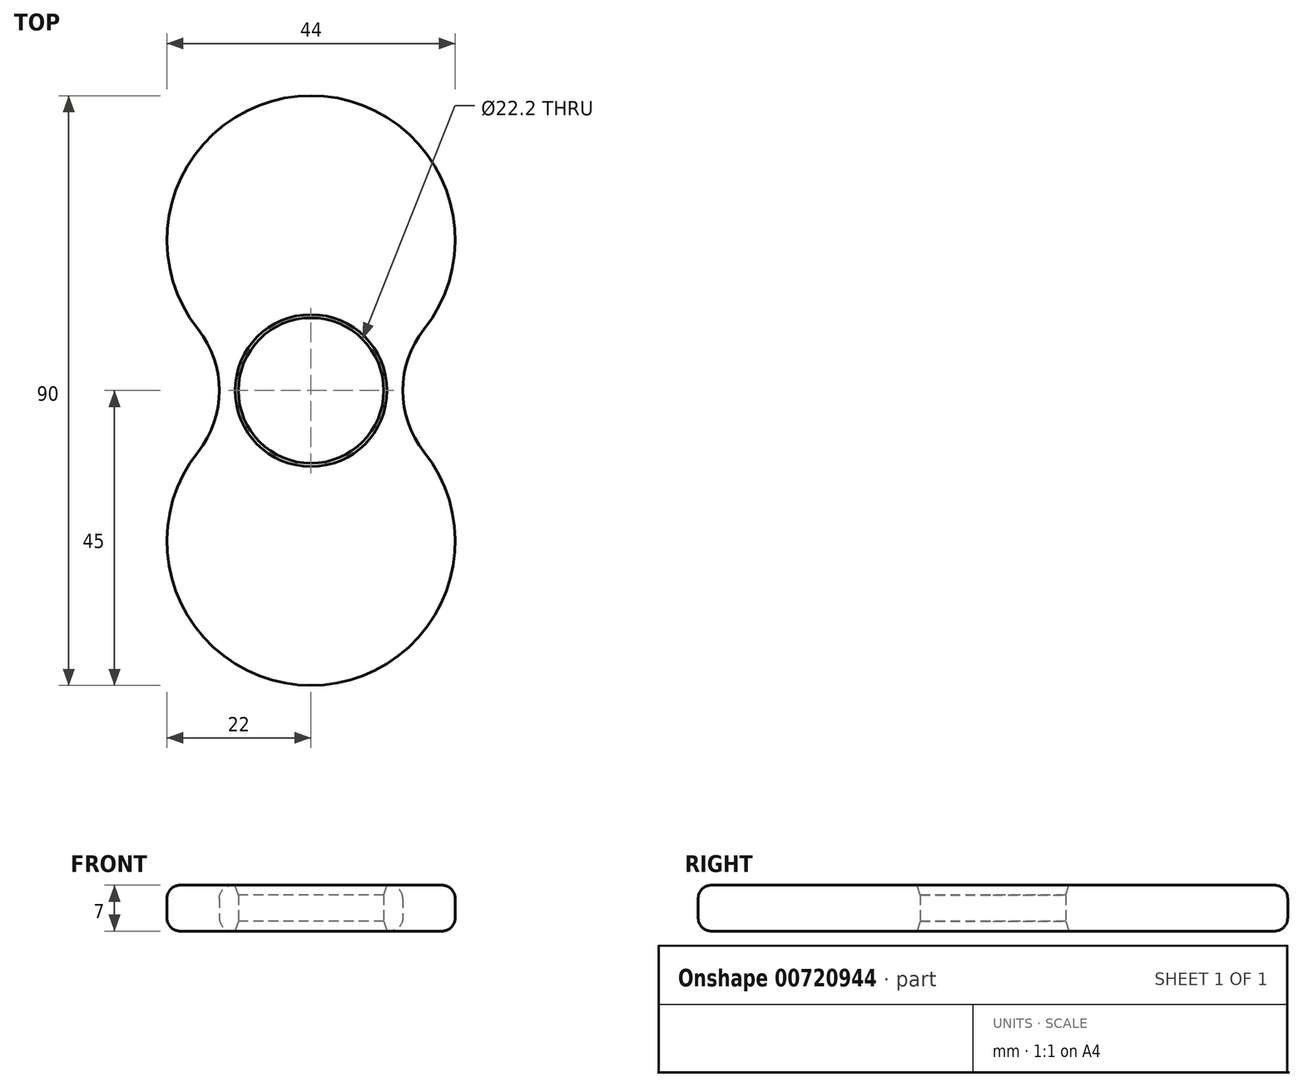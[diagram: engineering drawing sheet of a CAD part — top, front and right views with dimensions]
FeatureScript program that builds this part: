
annotation { "Feature Type Name" : "Feature", "Feature Type Description" : "" }
export const myFeature = defineFeature(function(context is Context, id is Id, definition is map)
    precondition{}
    {
        {
            var Q0;
            Q0=qCreatedBy(makeId("Top.planeOp"),FACE);
            var sketch = newSketch(context, id + "F0", { "sketchPlane" : qUnion([Q0])});
            skLineSegment(sketch, "E0", {"start": v(0, 0) * mm, "end": v(-28, 0) * mm, "construction": true});
            skArc(sketch, "E1", {"start": v(-31.25, -9.35) * mm, "mid": v(-28, 0) * mm, "end": v(-31.25, 9.35) * mm});
            skArc(sketch, "E2", {"start": v(3.25, 9.35) * mm, "mid": v(0, 0) * mm, "end": v(3.25, -9.35) * mm});
            skArc(sketch, "E3", {"start": v(3.25, 9.35) * mm, "mid": v(-14, 45) * mm, "end": v(-31.25, 9.35) * mm});
            skArc(sketch, "E4", {"start": v(-31.25, -9.35) * mm, "mid": v(-14, -45) * mm, "end": v(3.25, -9.35) * mm});
            skLineSegment(sketch, "E5", {"start": v(-36, 23) * mm, "end": v(8, 23) * mm, "construction": true});
            skLineSegment(sketch, "E6", {"start": v(-14, 45) * mm, "end": v(-14, -45) * mm, "construction": true});
            skCircle(sketch, "E7", {"center": v(-14, 0) * mm, "radius": 11.1 * mm});
            skSolve(sketch);
        }
        {
            var Q0;
            Q0=makeQuery(id+"F0.imprint","IMPRINT",FACE,{"disambiguationData":[TD([[makeQuery(id+"F0.imprint","IMPRINT",EDGE,{"derivedFrom":sQuery(id+"F0.wireOp",EDGE,"E1")}),-1.0]])]});
            extrude(context, id + "F1", {"entities" : qUnion([Q0]), "depth" : 7 * mm});
        }
        {
            var Q0;
            Q0=makeQuery(id+"F1.opExtrude","CAP_EDGE",EDGE,{"disambiguationData":[OSD([sQuery(id+"F0.wireOp",EDGE,"E7")])],"isStart":false});
            var Q1;
            Q1=makeQuery(id+"F1.opExtrude","CAP_EDGE",EDGE,{"disambiguationData":[OSD([sQuery(id+"F0.wireOp",EDGE,"E7")])],"isStart":true});
            chamfer(context, id + "F2", {"entities" : qUnion([Q0, Q1]), "chamferType" : ChamferType.TWO_OFFSETS, "width1" : 1.5 * mm, "oppositeDirection" : false, "width2" : .5 * mm, "tangentPropagation" : true});
        }
        {
            var Q0;
            Q0=makeQuery(id+"F1.opExtrude","CAP_EDGE",EDGE,{"disambiguationData":[OSD([sQuery(id+"F0.wireOp",EDGE,"E4")])],"isStart":false});
            var Q1;
            Q1=makeQuery(id+"F1.opExtrude","CAP_EDGE",EDGE,{"disambiguationData":[OSD([sQuery(id+"F0.wireOp",EDGE,"E4")])],"isStart":true});
            fillet(context, id + "F3", {"entities" : qUnion([Q0, Q1]), "radius" : 2 * mm, "tangentPropagation" : true, "allowEdgeOverflow" : false});
        }
    });
